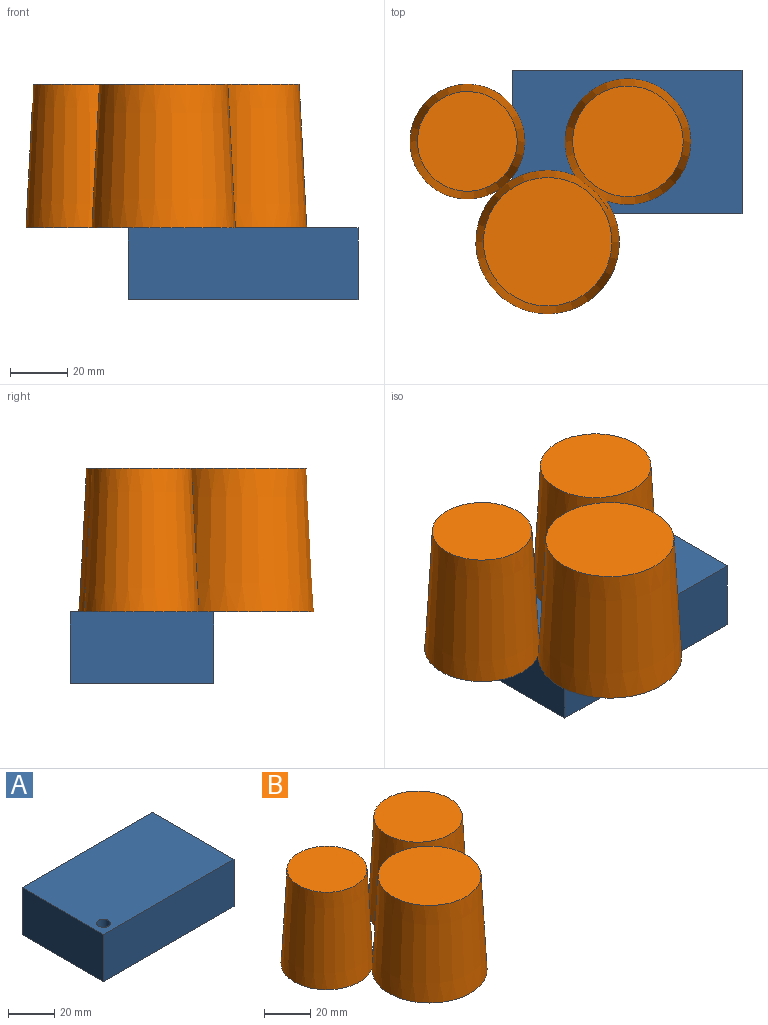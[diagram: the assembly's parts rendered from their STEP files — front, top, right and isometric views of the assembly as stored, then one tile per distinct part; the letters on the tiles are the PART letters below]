
ASSEMBLY  parts=2 mates=1
PART A: 7 faces, bbox 80x50x25 mm
  f0: plane 50x25mm, normal (-1,0,0), area 1250mm2, adj f1,f3,f4,f5
  f1: plane 80x25mm, normal (0,-1,0), area 2000mm2, adj f0,f2,f4,f5
  f2: plane 50x25mm, normal (1,0,0), area 1250mm2, adj f1,f3,f4,f5
  f3: plane 80x25mm, normal (0,1,0), area 2000mm2, adj f0,f2,f4,f5
  f4: plane 80x50mm, normal (0,0,1), area 3971.7mm2, adj f0,f1,f2,f3,f6
  f5: plane 80x50mm, normal (0,0,-1), area 3971.7mm2, adj f0,f1,f2,f3,f6
  f6: cylinder r=3mm len=25mm, axis (0,0,1), area 471.2mm2, adj f4,f5
PART B: 7 faces, bbox 97.8x81.9x50 mm
  f0: plane 34.76x34.76mm, normal (0,0,1), area 948.9mm2, adj f3
  f1: plane 38.53x38.53mm, normal (0,0,1), area 1166mm2, adj f2
  f2: cone r=21.89mm half-angle=3deg, axis (0,0,-1), area 6289.3mm2, adj f1,f4,f6
  f3: cone r=20mm half-angle=3deg, axis (0,0,-1), area 5874.6mm2, adj f0,f4,f6
  f4: cone r=25mm half-angle=3deg, axis (0,0,-1), area 7266mm2, adj f2,f3,f5,f6
  f5: plane 44.76x44.76mm, normal (0,0,1), area 1573.5mm2, adj f4
  f6: plane 97.84x81.89mm, normal (0,0,-1), area 4705.2mm2, adj f2,f3,f4
PLACE A at identity
PLACE B t=(53.23,25.14,25)mm
MATE planar B.f2 <-> A.f4  axis (0,0,-1) through (40.24,25.14,25)mm
